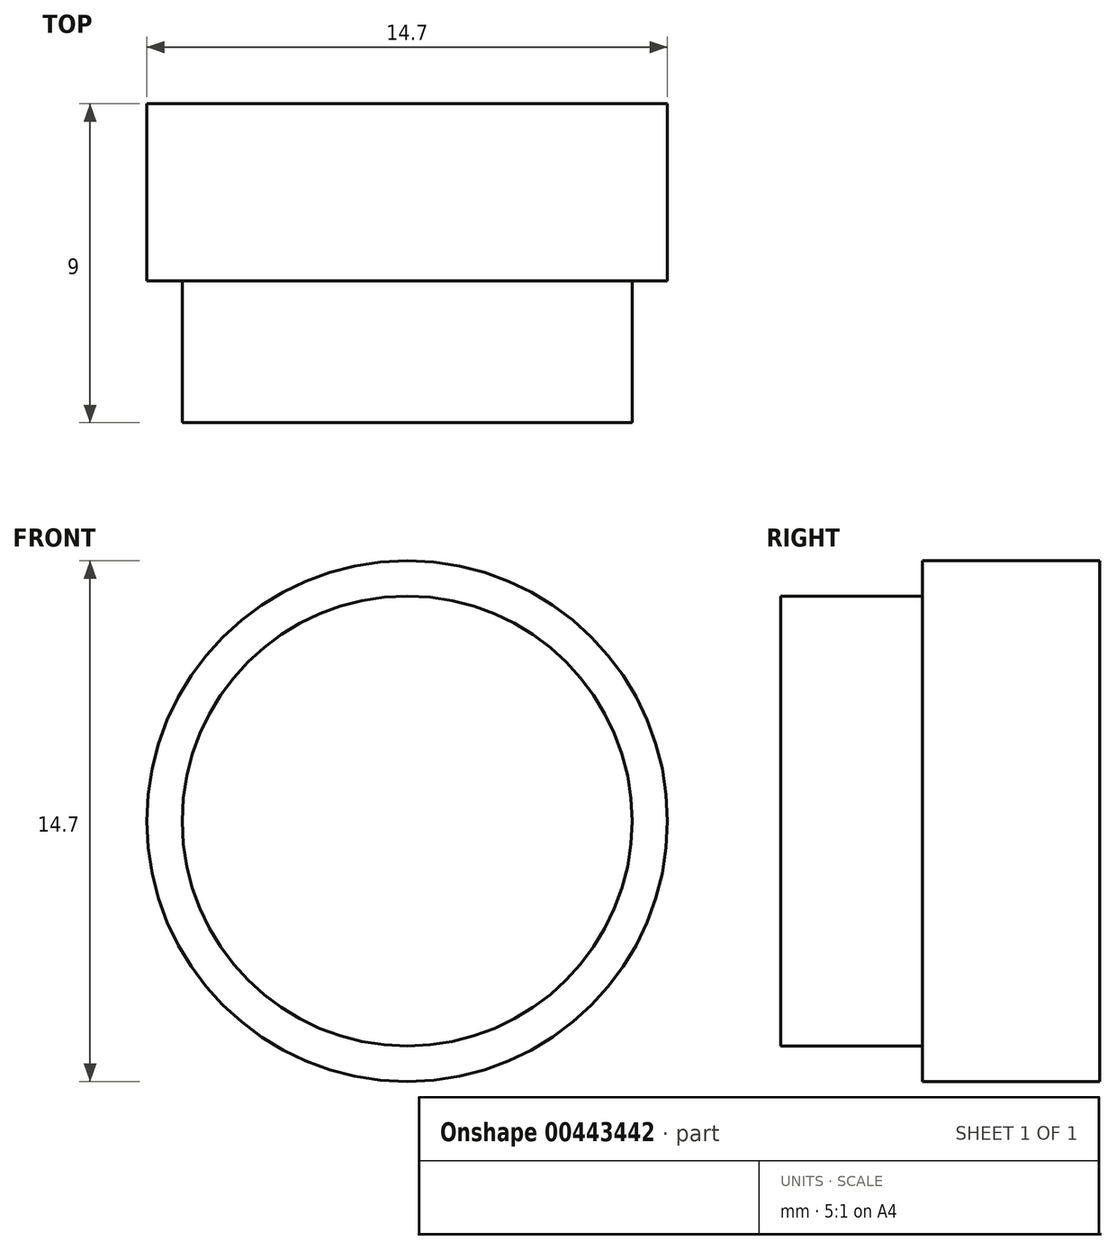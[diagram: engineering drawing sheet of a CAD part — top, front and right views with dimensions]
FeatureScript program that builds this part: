
annotation { "Feature Type Name" : "Feature", "Feature Type Description" : "" }
export const myFeature = defineFeature(function(context is Context, id is Id, definition is map)
    precondition{}
    {
        {
            var Q0;
            Q0=qCreatedBy(makeId("Front.planeOp"),FACE);
            var sketch = newSketch(context, id + "F0", { "sketchPlane" : qUnion([Q0])});
            skCircle(sketch, "E0", {"center": v(0, 0) * mm, "radius": 6.35 * mm});
            skSolve(sketch);
        }
        {
            var Q0;
            Q0 = qSketchRegion(id + "F0", true);
            extrude(context, id + "F1", {"entities" : qUnion([Q0]), "depth" : 4 * mm});
        }
        {
            var Q0;
            Q0=qCreatedBy(makeId("Front.planeOp"),FACE);
            var sketch = newSketch(context, id + "F2", { "sketchPlane" : qUnion([Q0])});
            skCircle(sketch, "E1", {"center": v(0, 0) * mm, "radius": 7.35 * mm});
            skSolve(sketch);
        }
        {
            var Q0;
            Q0=makeQuery(id+"F2.imprint","IMPRINT",FACE,{"disambiguationData":[TD([[makeQuery(id+"F2.imprint","IMPRINT",EDGE,{"derivedFrom":sQuery(id+"F2.wireOp",EDGE,"E1")}),1.0]])]});
            extrude(context, id + "F3", {"entities" : qUnion([Q0]), "operationType" : NewBodyOperationType.ADD, "oppositeDirection" : true, "depth" : 5 * mm});
        }
    });
